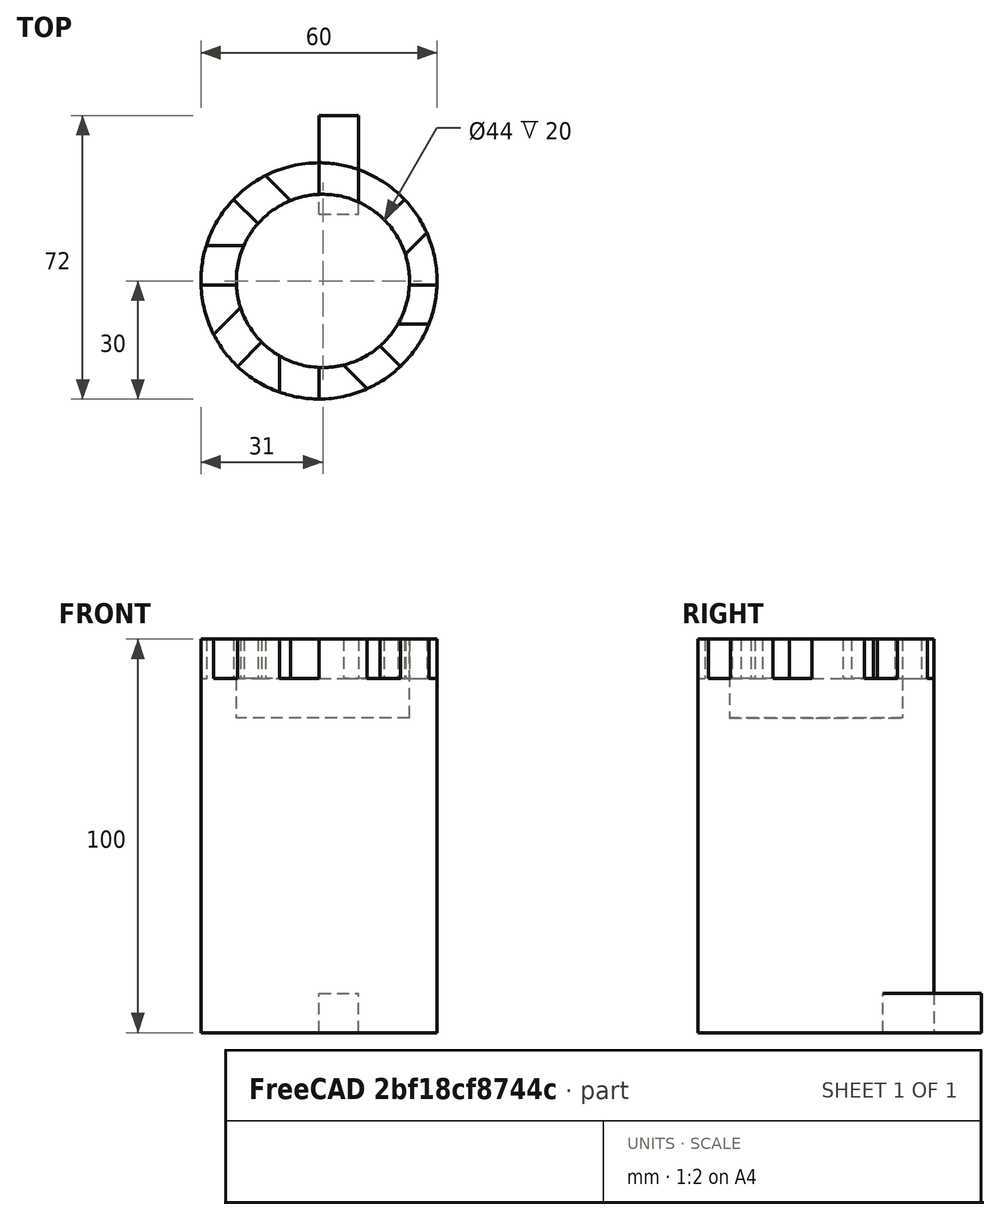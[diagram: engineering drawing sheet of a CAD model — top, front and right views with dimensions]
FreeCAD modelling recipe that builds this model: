
FCSTD DOCUMENT  (FreeCAD 1.0R39319 (Git))
Label: ojt1_t11r03_tower
License: All rights reserved
LicenseURL: https://en.wikipedia.org/wiki/All_rights_reserved
objects: Part::Cylinder×2, Part::Cut×2, Part::Box×1, Part::FeaturePython×1
note: 5 computed .brp shape members not serialized (recipe doc carries the construction recipe); baked Part::Feature solids carry a one-line shape summary decoded from their .brp

FEATURE [Part::Box] Box  label="Cub"
  AttacherType = Attacher::AttachEngine3D
  Height = 10
  Length = 10
  Width = 25
FEATURE [Part::FeaturePython] Array  # Draft array (typed FeaturePython)
  AlwaysSyncPlacement = false
  Angle = 360
  ArrayType = 1
  Axis = (0,0,1)
  Base = -> Box
  Center = (0,-18,0)
  Count = 8
  ExpandArray = false
  Fuse = false
  IntervalAxis = (0,0,0)
  IntervalX = (100,0,0)
  IntervalY = (0,100,0)
  IntervalZ = (0,0,100)
  NumberCircles = 3
  NumberPolar = 8
  NumberX = 2
  NumberY = 2
  NumberZ = 1
  Placement = pos=(0,0,90) rot=(0,0,1;0rad)
  PlacementList = 8 placements: [(0,0,0),(-12.7279,-5.27208,0),(-18,-18,0),(-12.7279,-30.7279,0),(-2.20436e-15,-36,0),(12.7279,-30.7279,0),(18,-18,0),(12.7279,-5.27208,0)]
  RadialDistance = 50
  ScaleList = (8) [(1,1,1),(1,1,1),(1,1,1),(1,1,1),(1,1,1),(1,1,1),(1,1,1),(1,1,1)]
  Symmetry = 1
  TangentialDistance = 25
FEATURE [Part::Cylinder] Cylinder  label="Cilindre"
  Angle = 360
  AttacherType = Attacher::AttachEngine3D
  FirstAngle = 0
  Height = 100
  Placement = pos=(0,-17,0) rot=(0,0,1;0rad)
  Radius = 30
  SecondAngle = 0
FEATURE [Part::Cut] Cut
  Base = -> Cylinder
  Refine = true
  Tool = -> Array
FEATURE [Part::Cylinder] Cylinder001  label="Cilindre001"
  Angle = 360
  AttacherType = Attacher::AttachEngine3D
  FirstAngle = 0
  Height = 20
  Placement = pos=(1,-17,80) rot=(0,0,1;0rad)
  Radius = 22
  SecondAngle = 0
FEATURE [Part::Cut] Cut001
  Base = -> Cut
  Refine = true
  Tool = -> Cylinder001
